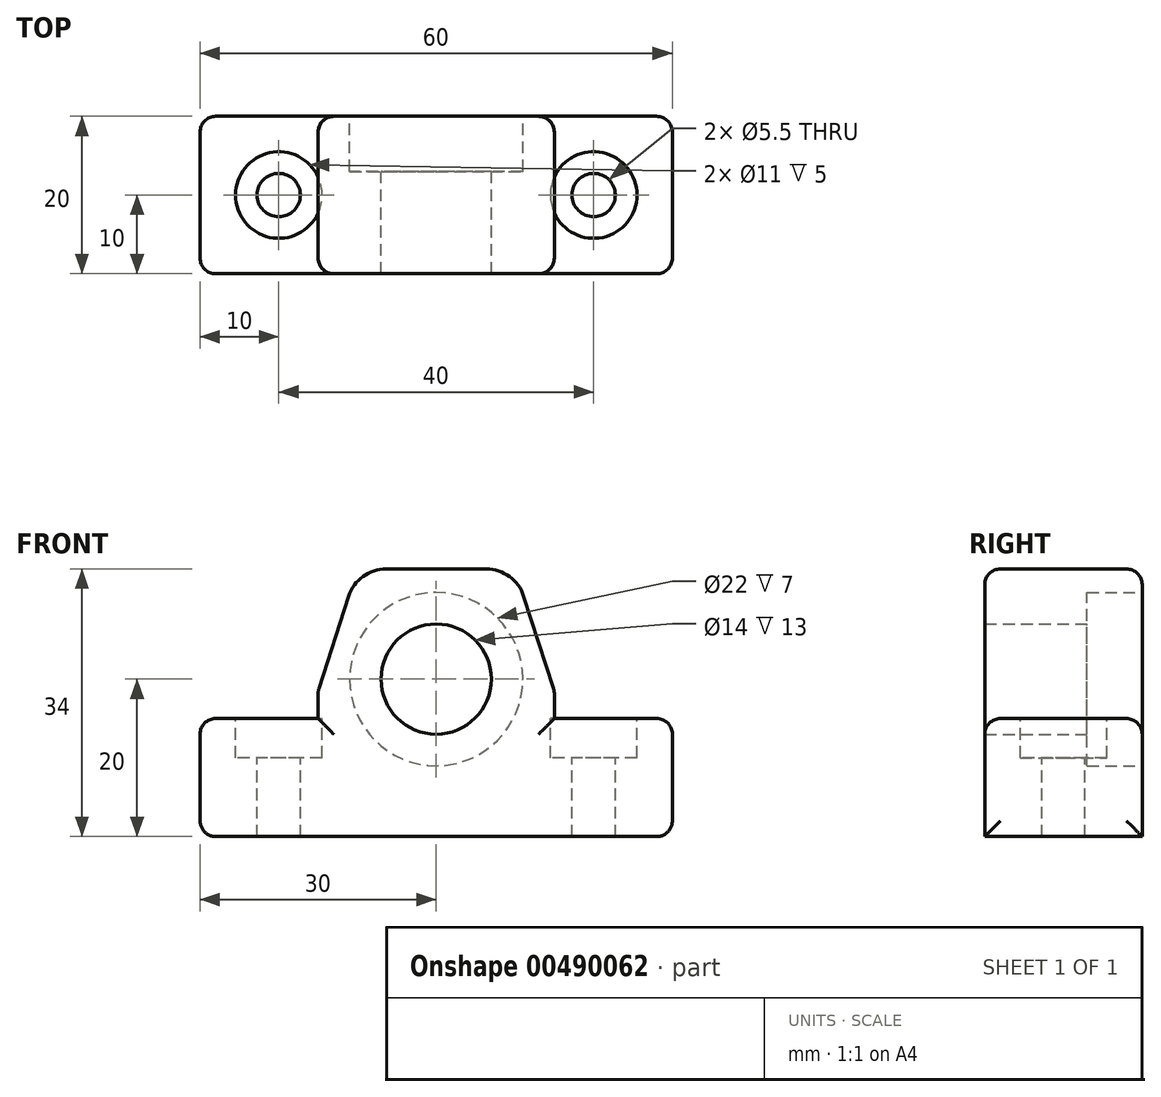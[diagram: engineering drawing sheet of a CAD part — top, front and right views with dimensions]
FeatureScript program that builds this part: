
annotation { "Feature Type Name" : "Feature", "Feature Type Description" : "" }
export const myFeature = defineFeature(function(context is Context, id is Id, definition is map)
    precondition{}
    {
        {
            var Q0;
            Q0=qCreatedBy(makeId("Front.planeOp"),FACE);
            var sketch = newSketch(context, id + "F0", { "sketchPlane" : qUnion([Q0])});
            skLineSegment(sketch, "E0", {"start": v(-30, -15) * mm, "end": v(30, -15) * mm});
            skLineSegment(sketch, "E1", {"start": v(30, -15) * mm, "end": v(30, 0) * mm});
            skLineSegment(sketch, "E2", {"start": v(30, 0) * mm, "end": v(15, 0) * mm});
            skLineSegment(sketch, "E3", {"start": v(15, 0) * mm, "end": v(15, 3.5) * mm});
            skLineSegment(sketch, "E4", {"start": v(15, 3.5) * mm, "end": v(10, 19) * mm});
            skLineSegment(sketch, "E5", {"start": v(10, 19) * mm, "end": v(-10, 19) * mm});
            skLineSegment(sketch, "E6", {"start": v(-10, 19) * mm, "end": v(-15, 3.5) * mm});
            skLineSegment(sketch, "E7", {"start": v(-15, 3.5) * mm, "end": v(-15, 0) * mm});
            skLineSegment(sketch, "E8", {"start": v(-15, 0) * mm, "end": v(-30, 0) * mm});
            skLineSegment(sketch, "E9", {"start": v(-30, 0) * mm, "end": v(-30, -15) * mm});
            skCircle(sketch, "E10", {"center": v(0, 5) * mm, "radius": 11 * mm});
            skSolve(sketch);
        }
        {
            var Q0;
            Q0 = qSketchRegion(id + "F0", true);
            extrude(context, id + "F1", {"entities" : qUnion([Q0]), "depth" : 10 * mm, "hasSecondDirection" : true, "secondDirectionOppositeDirection" : true, "secondDirectionDepth" : 10 * mm});
        }
        {
            var Q0;
            Q0=qCreatedBy(makeId("Front.planeOp"),FACE);
            var sketch = newSketch(context, id + "F2", { "sketchPlane" : qUnion([Q0])});
            skCircle(sketch, "E11", {"center": v(0, 5) * mm, "radius": 7 * mm});
            skCircle(sketch, "E12", {"center": v(0, 5) * mm, "radius": 11 * mm});
            skPoint(sketch, "E13", {"position": v(20, 0) * mm});
            skPoint(sketch, "E14", {"position": v(-20, 0) * mm});
            skSolve(sketch);
        }
        {
            var Q0;
            Q0=makeQuery(id+"F2.imprint","IMPRINT",FACE,{"disambiguationData":[TD([[makeQuery(id+"F2.imprint","IMPRINT",EDGE,{"derivedFrom":sQuery(id+"F2.wireOp",EDGE,"E11")}),-1.0]])]});
            extrude(context, id + "F3", {"entities" : qUnion([Q0]), "operationType" : NewBodyOperationType.ADD, "depth" : 10 * mm, "hasSecondDirection" : true, "secondDirectionOppositeDirection" : true, "secondDirectionDepth" : 3 * mm});
        }
        {
            var Q0;
            Q0=qCreatedBy(makeId("Top.planeOp"),FACE);
            var sketch = newSketch(context, id + "F4", { "sketchPlane" : qUnion([Q0])});
            skPoint(sketch, "E15", {"position": v(-20, 0) * mm});
            skPoint(sketch, "E16", {"position": v(20, 0) * mm});
            skSolve(sketch);
        }
        {
            var Q0;
            Q0=sQuery(id+"F4.wireOp",VERTEX,"E15");
            var Q1;
            Q1=sQuery(id+"F4.wireOp",VERTEX,"E16");
            var Q2;
            Q2=makeQuery(id+"F1.opExtrude","SWEPT_BODY",BODY,{"disambiguationData":[OSD([sQuery(id+"F0.wireOp",EDGE,"E0"),sQuery(id+"F0.wireOp",EDGE,"E1"),sQuery(id+"F0.wireOp",EDGE,"E2"),sQuery(id+"F0.wireOp",EDGE,"E3"),sQuery(id+"F0.wireOp",EDGE,"E4"),sQuery(id+"F0.wireOp",EDGE,"E5"),sQuery(id+"F0.wireOp",EDGE,"E6"),sQuery(id+"F0.wireOp",EDGE,"E7"),sQuery(id+"F0.wireOp",EDGE,"E8"),sQuery(id+"F0.wireOp",EDGE,"E9"),sQuery(id+"F0.wireOp",EDGE,"E10")])]});
            hole(context, id + "F5", {"style" : HoleStyle.C_BORE, "endStyle" : HoleEndStyle.THROUGH, "holeDiameter" : 5.5 * mm, "cBoreDiameter" : 11 * mm, "cBoreDepth" : 5 * mm, "isTappedThrough" : true, "tappedDepth" : 12 * mm, "tapClearance" : 3, "locations" : qUnion([Q0, Q1]), "scope" : qUnion([Q2])});
        }
        {
            var Q0;
            Q0=makeQuery(id+"F1.opExtrude","SWEPT_EDGE",EDGE,{"disambiguationData":[OSD([sQuery(id+"F0.wireOp",EDGE,"E4"),sQuery(id+"F0.wireOp",EDGE,"E5")])]});
            var Q1;
            Q1=makeQuery(id+"F1.opExtrude","SWEPT_EDGE",EDGE,{"disambiguationData":[OSD([sQuery(id+"F0.wireOp",EDGE,"E5"),sQuery(id+"F0.wireOp",EDGE,"E6")])]});
            fillet(context, id + "F6", {"entities" : qUnion([Q0, Q1]), "radius" : 5 * mm, "tangentPropagation" : true, "allowEdgeOverflow" : false});
        }
        {
            var Q0;
            Q0=makeQuery(id+"F1.opExtrude","SWEPT_FACE",FACE,{"disambiguationData":[OSD([sQuery(id+"F0.wireOp",EDGE,"E9")])]});
            var Q1;
            Q1=makeQuery(id+"F1.opExtrude","CAP_EDGE",EDGE,{"disambiguationData":[OSD([sQuery(id+"F0.wireOp",EDGE,"E8")])],"isStart":true});
            var Q2;
            Q2=makeQuery(id+"F1.opExtrude","SWEPT_EDGE",EDGE,{"disambiguationData":[OSD([sQuery(id+"F0.wireOp",EDGE,"E6"),sQuery(id+"F0.wireOp",EDGE,"E7")])]});
            var Q3;
            Q3=makeQuery(id+"F1.opExtrude","SWEPT_EDGE",EDGE,{"disambiguationData":[OSD([sQuery(id+"F0.wireOp",EDGE,"E3"),sQuery(id+"F0.wireOp",EDGE,"E4")])]});
            var Q4;
            Q4=makeQuery(id+"F1.opExtrude","SWEPT_EDGE",EDGE,{"disambiguationData":[OSD([sQuery(id+"F0.wireOp",EDGE,"E0"),sQuery(id+"F0.wireOp",EDGE,"E1")])]});
            var Q5;
            Q5=makeQuery(id+"F1.opExtrude","CAP_EDGE",EDGE,{"disambiguationData":[OSD([sQuery(id+"F0.wireOp",EDGE,"E1")])],"isStart":false});
            var Q6;
            Q6=makeQuery(id+"F1.opExtrude","SWEPT_EDGE",EDGE,{"disambiguationData":[OSD([sQuery(id+"F0.wireOp",EDGE,"E1"),sQuery(id+"F0.wireOp",EDGE,"E2")])]});
            var Q7;
            Q7=makeQuery(id+"F1.opExtrude","CAP_EDGE",EDGE,{"disambiguationData":[OSD([sQuery(id+"F0.wireOp",EDGE,"E1")])],"isStart":true});
            var Q8;
            Q8=makeQuery(id+"F1.opExtrude","CAP_EDGE",EDGE,{"disambiguationData":[OSD([sQuery(id+"F0.wireOp",EDGE,"E2")])],"isStart":true});
            var Q9;
            {var subQ0=sQuery(id+"F0.wireOp",EDGE,"E5");var subQ1=sQuery(id+"F0.wireOp",EDGE,"E4");Q9=makeQuery(id+"F6.opFillet","BLEND_EDGE",EDGE,{"blendedFrom":[makeQuery(id+"F1.opExtrude","SWEPT_EDGE",EDGE,{"disambiguationData":[OSD([subQ1,subQ0])]}),makeQuery(id+"F1.opExtrude","CAP_FACE",FACE,{"disambiguationData":[OSD([sQuery(id+"F0.wireOp",EDGE,"E0"),sQuery(id+"F0.wireOp",EDGE,"E1"),sQuery(id+"F0.wireOp",EDGE,"E2"),sQuery(id+"F0.wireOp",EDGE,"E3"),subQ1,subQ0,sQuery(id+"F0.wireOp",EDGE,"E6"),sQuery(id+"F0.wireOp",EDGE,"E7"),sQuery(id+"F0.wireOp",EDGE,"E8"),sQuery(id+"F0.wireOp",EDGE,"E9"),sQuery(id+"F0.wireOp",EDGE,"E10")])],"isStart":true})],"blendedInto":[makeQuery(id+"F1.opExtrude","CAP_FACE",FACE,{"disambiguationData":[OSD([sQuery(id+"F0.wireOp",EDGE,"E0"),sQuery(id+"F0.wireOp",EDGE,"E1"),sQuery(id+"F0.wireOp",EDGE,"E2"),sQuery(id+"F0.wireOp",EDGE,"E3"),subQ1,subQ0,sQuery(id+"F0.wireOp",EDGE,"E6"),sQuery(id+"F0.wireOp",EDGE,"E7"),sQuery(id+"F0.wireOp",EDGE,"E8"),sQuery(id+"F0.wireOp",EDGE,"E9"),sQuery(id+"F0.wireOp",EDGE,"E10")])],"isStart":true})]});}
            var Q10;
            Q10=makeQuery(id+"F1.opExtrude","CAP_EDGE",EDGE,{"disambiguationData":[OSD([sQuery(id+"F0.wireOp",EDGE,"E4")])],"isStart":true});
            var Q11;
            Q11=makeQuery(id+"F1.opExtrude","CAP_EDGE",EDGE,{"disambiguationData":[OSD([sQuery(id+"F0.wireOp",EDGE,"E3")])],"isStart":true});
            var Q12;
            Q12=makeQuery(id+"F1.opExtrude","CAP_EDGE",EDGE,{"disambiguationData":[OSD([sQuery(id+"F0.wireOp",EDGE,"E5")])],"isStart":true});
            var Q13;
            {var subQ0=sQuery(id+"F0.wireOp",EDGE,"E6");var subQ1=sQuery(id+"F0.wireOp",EDGE,"E5");Q13=makeQuery(id+"F6.opFillet","BLEND_EDGE",EDGE,{"blendedFrom":[makeQuery(id+"F1.opExtrude","SWEPT_EDGE",EDGE,{"disambiguationData":[OSD([subQ1,subQ0])]}),makeQuery(id+"F1.opExtrude","CAP_FACE",FACE,{"disambiguationData":[OSD([sQuery(id+"F0.wireOp",EDGE,"E0"),sQuery(id+"F0.wireOp",EDGE,"E1"),sQuery(id+"F0.wireOp",EDGE,"E2"),sQuery(id+"F0.wireOp",EDGE,"E3"),sQuery(id+"F0.wireOp",EDGE,"E4"),subQ1,subQ0,sQuery(id+"F0.wireOp",EDGE,"E7"),sQuery(id+"F0.wireOp",EDGE,"E8"),sQuery(id+"F0.wireOp",EDGE,"E9"),sQuery(id+"F0.wireOp",EDGE,"E10")])],"isStart":true})],"blendedInto":[makeQuery(id+"F1.opExtrude","CAP_FACE",FACE,{"disambiguationData":[OSD([sQuery(id+"F0.wireOp",EDGE,"E0"),sQuery(id+"F0.wireOp",EDGE,"E1"),sQuery(id+"F0.wireOp",EDGE,"E2"),sQuery(id+"F0.wireOp",EDGE,"E3"),sQuery(id+"F0.wireOp",EDGE,"E4"),subQ1,subQ0,sQuery(id+"F0.wireOp",EDGE,"E7"),sQuery(id+"F0.wireOp",EDGE,"E8"),sQuery(id+"F0.wireOp",EDGE,"E9"),sQuery(id+"F0.wireOp",EDGE,"E10")])],"isStart":true})]});}
            var Q14;
            Q14=makeQuery(id+"F1.opExtrude","CAP_EDGE",EDGE,{"disambiguationData":[OSD([sQuery(id+"F0.wireOp",EDGE,"E6")])],"isStart":true});
            var Q15;
            Q15=makeQuery(id+"F1.opExtrude","CAP_EDGE",EDGE,{"disambiguationData":[OSD([sQuery(id+"F0.wireOp",EDGE,"E7")])],"isStart":true});
            var Q16;
            Q16=makeQuery(id+"F1.opExtrude","CAP_EDGE",EDGE,{"disambiguationData":[OSD([sQuery(id+"F0.wireOp",EDGE,"E8")])],"isStart":false});
            var Q17;
            Q17=makeQuery(id+"F1.opExtrude","CAP_EDGE",EDGE,{"disambiguationData":[OSD([sQuery(id+"F0.wireOp",EDGE,"E7")])],"isStart":false});
            var Q18;
            Q18=makeQuery(id+"F1.opExtrude","CAP_EDGE",EDGE,{"disambiguationData":[OSD([sQuery(id+"F0.wireOp",EDGE,"E6")])],"isStart":false});
            var Q19;
            {var subQ0=sQuery(id+"F0.wireOp",EDGE,"E6");var subQ1=sQuery(id+"F0.wireOp",EDGE,"E5");Q19=makeQuery(id+"F6.opFillet","BLEND_EDGE",EDGE,{"blendedFrom":[makeQuery(id+"F1.opExtrude","SWEPT_EDGE",EDGE,{"disambiguationData":[OSD([subQ1,subQ0])]}),makeQuery(id+"F3.boolean.opBoolean","MERGE",FACE,{"derivedFrom":[makeQuery(id+"F1.opExtrude","CAP_FACE",FACE,{"disambiguationData":[OSD([sQuery(id+"F0.wireOp",EDGE,"E0"),sQuery(id+"F0.wireOp",EDGE,"E1"),sQuery(id+"F0.wireOp",EDGE,"E2"),sQuery(id+"F0.wireOp",EDGE,"E3"),sQuery(id+"F0.wireOp",EDGE,"E4"),subQ1,subQ0,sQuery(id+"F0.wireOp",EDGE,"E7"),sQuery(id+"F0.wireOp",EDGE,"E8"),sQuery(id+"F0.wireOp",EDGE,"E9"),sQuery(id+"F0.wireOp",EDGE,"E10")])],"isStart":false}),makeQuery(id+"F3.opExtrude","CAP_FACE",FACE,{"disambiguationData":[OSD([sQuery(id+"F2.wireOp",EDGE,"E11"),sQuery(id+"F2.wireOp",EDGE,"E12")])],"isStart":false})]})],"blendedInto":[makeQuery(id+"F3.boolean.opBoolean","MERGE",FACE,{"derivedFrom":[makeQuery(id+"F1.opExtrude","CAP_FACE",FACE,{"disambiguationData":[OSD([sQuery(id+"F0.wireOp",EDGE,"E0"),sQuery(id+"F0.wireOp",EDGE,"E1"),sQuery(id+"F0.wireOp",EDGE,"E2"),sQuery(id+"F0.wireOp",EDGE,"E3"),sQuery(id+"F0.wireOp",EDGE,"E4"),subQ1,subQ0,sQuery(id+"F0.wireOp",EDGE,"E7"),sQuery(id+"F0.wireOp",EDGE,"E8"),sQuery(id+"F0.wireOp",EDGE,"E9"),sQuery(id+"F0.wireOp",EDGE,"E10")])],"isStart":false}),makeQuery(id+"F3.opExtrude","CAP_FACE",FACE,{"disambiguationData":[OSD([sQuery(id+"F2.wireOp",EDGE,"E11"),sQuery(id+"F2.wireOp",EDGE,"E12")])],"isStart":false})]})]});}
            var Q20;
            Q20=makeQuery(id+"F1.opExtrude","CAP_EDGE",EDGE,{"disambiguationData":[OSD([sQuery(id+"F0.wireOp",EDGE,"E5")])],"isStart":false});
            var Q21;
            {var subQ0=sQuery(id+"F0.wireOp",EDGE,"E5");var subQ1=sQuery(id+"F0.wireOp",EDGE,"E4");Q21=makeQuery(id+"F6.opFillet","BLEND_EDGE",EDGE,{"blendedFrom":[makeQuery(id+"F1.opExtrude","SWEPT_EDGE",EDGE,{"disambiguationData":[OSD([subQ1,subQ0])]}),makeQuery(id+"F3.boolean.opBoolean","MERGE",FACE,{"derivedFrom":[makeQuery(id+"F1.opExtrude","CAP_FACE",FACE,{"disambiguationData":[OSD([sQuery(id+"F0.wireOp",EDGE,"E0"),sQuery(id+"F0.wireOp",EDGE,"E1"),sQuery(id+"F0.wireOp",EDGE,"E2"),sQuery(id+"F0.wireOp",EDGE,"E3"),subQ1,subQ0,sQuery(id+"F0.wireOp",EDGE,"E6"),sQuery(id+"F0.wireOp",EDGE,"E7"),sQuery(id+"F0.wireOp",EDGE,"E8"),sQuery(id+"F0.wireOp",EDGE,"E9"),sQuery(id+"F0.wireOp",EDGE,"E10")])],"isStart":false}),makeQuery(id+"F3.opExtrude","CAP_FACE",FACE,{"disambiguationData":[OSD([sQuery(id+"F2.wireOp",EDGE,"E11"),sQuery(id+"F2.wireOp",EDGE,"E12")])],"isStart":false})]})],"blendedInto":[makeQuery(id+"F3.boolean.opBoolean","MERGE",FACE,{"derivedFrom":[makeQuery(id+"F1.opExtrude","CAP_FACE",FACE,{"disambiguationData":[OSD([sQuery(id+"F0.wireOp",EDGE,"E0"),sQuery(id+"F0.wireOp",EDGE,"E1"),sQuery(id+"F0.wireOp",EDGE,"E2"),sQuery(id+"F0.wireOp",EDGE,"E3"),subQ1,subQ0,sQuery(id+"F0.wireOp",EDGE,"E6"),sQuery(id+"F0.wireOp",EDGE,"E7"),sQuery(id+"F0.wireOp",EDGE,"E8"),sQuery(id+"F0.wireOp",EDGE,"E9"),sQuery(id+"F0.wireOp",EDGE,"E10")])],"isStart":false}),makeQuery(id+"F3.opExtrude","CAP_FACE",FACE,{"disambiguationData":[OSD([sQuery(id+"F2.wireOp",EDGE,"E11"),sQuery(id+"F2.wireOp",EDGE,"E12")])],"isStart":false})]})]});}
            var Q22;
            Q22=makeQuery(id+"F1.opExtrude","CAP_EDGE",EDGE,{"disambiguationData":[OSD([sQuery(id+"F0.wireOp",EDGE,"E4")])],"isStart":false});
            var Q23;
            Q23=makeQuery(id+"F1.opExtrude","CAP_EDGE",EDGE,{"disambiguationData":[OSD([sQuery(id+"F0.wireOp",EDGE,"E3")])],"isStart":false});
            var Q24;
            Q24=makeQuery(id+"F1.opExtrude","CAP_EDGE",EDGE,{"disambiguationData":[OSD([sQuery(id+"F0.wireOp",EDGE,"E2")])],"isStart":false});
            fillet(context, id + "F7", {"entities" : qUnion([Q0, Q1, Q2, Q3, Q4, Q5, Q6, Q7, Q8, Q9, Q10, Q11, Q12, Q13, Q14, Q15, Q16, Q17, Q18, Q19, Q20, Q21, Q22, Q23, Q24]), "radius" : 2 * mm, "tangentPropagation" : true, "allowEdgeOverflow" : false});
        }
    });
